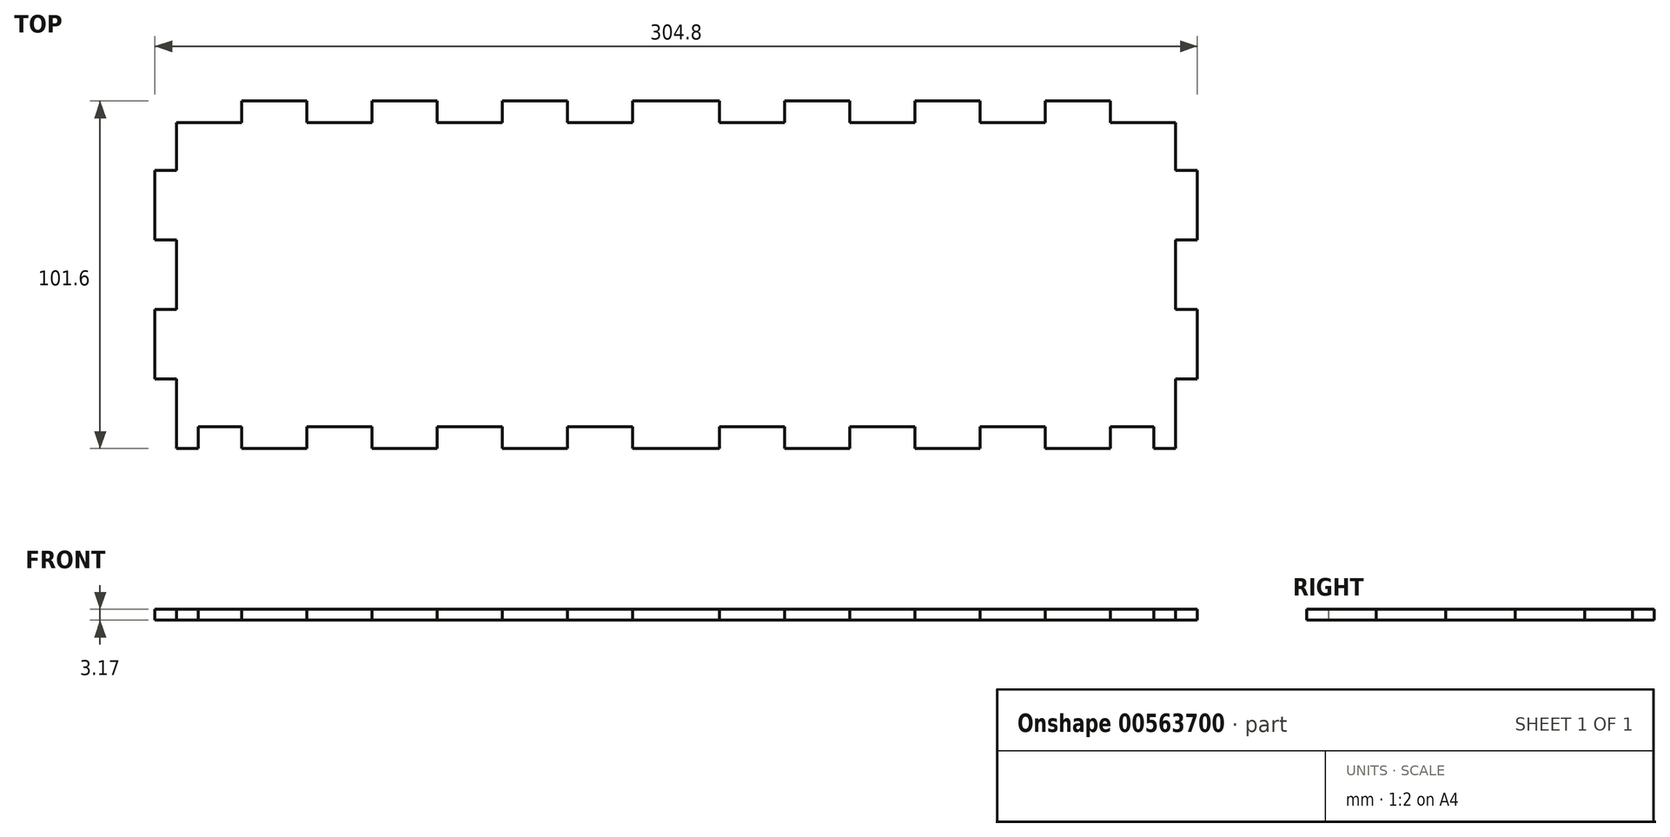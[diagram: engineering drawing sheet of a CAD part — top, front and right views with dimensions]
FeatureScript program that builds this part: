
annotation { "Feature Type Name" : "Feature", "Feature Type Description" : "" }
export const myFeature = defineFeature(function(context is Context, id is Id, definition is map)
    precondition{}
    {
        {
            var Q0;
            Q0=qCreatedBy(makeId("Top.planeOp"),FACE);
            var sketch = newSketch(context, id + "F0", { "sketchPlane" : qUnion([Q0])});
            skLineSegment(sketch, "E0", {"start": v(24.27, -64.8) * mm, "end": v(24.27, -44.49) * mm});
            skLineSegment(sketch, "E1", {"start": v(24.27, -44.49) * mm, "end": v(17.92, -44.49) * mm});
            skLineSegment(sketch, "E2", {"start": v(17.92, -44.49) * mm, "end": v(17.92, -24.17) * mm});
            skLineSegment(sketch, "E3", {"start": v(17.92, -24.17) * mm, "end": v(24.27, -24.17) * mm});
            skLineSegment(sketch, "E4", {"start": v(24.27, -24.17) * mm, "end": v(24.27, -3.85) * mm});
            skLineSegment(sketch, "E5", {"start": v(24.27, -3.85) * mm, "end": v(17.92, -3.85) * mm});
            skLineSegment(sketch, "E6", {"start": v(17.92, -3.85) * mm, "end": v(17.92, 16.47) * mm});
            skLineSegment(sketch, "E7", {"start": v(17.92, 16.47) * mm, "end": v(24.27, 16.47) * mm});
            skLineSegment(sketch, "E8", {"start": v(24.27, 16.47) * mm, "end": v(24.27, 30.44) * mm});
            skLineSegment(sketch, "E9", {"start": v(24.27, 30.44) * mm, "end": v(43.32, 30.44) * mm});
            skLineSegment(sketch, "E10", {"start": v(43.32, 30.44) * mm, "end": v(43.32, 36.8) * mm});
            skLineSegment(sketch, "E11", {"start": v(43.32, 36.8) * mm, "end": v(62.37, 36.8) * mm});
            skLineSegment(sketch, "E12", {"start": v(62.37, 36.8) * mm, "end": v(62.37, 30.44) * mm});
            skLineSegment(sketch, "E13", {"start": v(62.37, 30.44) * mm, "end": v(81.42, 30.44) * mm});
            skLineSegment(sketch, "E14", {"start": v(81.42, 30.44) * mm, "end": v(81.42, 36.8) * mm});
            skLineSegment(sketch, "E15", {"start": v(81.42, 36.8) * mm, "end": v(100.47, 36.8) * mm});
            skLineSegment(sketch, "E16", {"start": v(100.47, 36.8) * mm, "end": v(100.47, 30.44) * mm});
            skLineSegment(sketch, "E17", {"start": v(100.47, 30.44) * mm, "end": v(119.52, 30.44) * mm});
            skLineSegment(sketch, "E18", {"start": v(119.52, 30.44) * mm, "end": v(119.52, 36.8) * mm});
            skLineSegment(sketch, "E19", {"start": v(119.52, 36.8) * mm, "end": v(138.57, 36.8) * mm});
            skLineSegment(sketch, "E20", {"start": v(138.57, 36.8) * mm, "end": v(138.57, 30.44) * mm});
            skLineSegment(sketch, "E21", {"start": v(138.57, 30.44) * mm, "end": v(157.62, 30.44) * mm});
            skLineSegment(sketch, "E22", {"start": v(157.62, 30.44) * mm, "end": v(157.62, 36.8) * mm});
            skLineSegment(sketch, "E23", {"start": v(157.62, 36.8) * mm, "end": v(170.32, 36.8) * mm});
            skLineSegment(sketch, "E24", {"start": v(170.32, 36.8) * mm, "end": v(170.32, -64.8) * mm, "construction": true});
            skLineSegment(sketch, "E25.MirrorCS", {"start": v(240.17, 36.8) * mm, "end": v(240.17, 30.44) * mm});
            skLineSegment(sketch, "E26.MirrorCS", {"start": v(322.72, 16.47) * mm, "end": v(316.37, 16.47) * mm});
            skLineSegment(sketch, "E27.MirrorCS", {"start": v(316.37, -3.85) * mm, "end": v(322.72, -3.85) * mm});
            skLineSegment(sketch, "E28.MirrorCS", {"start": v(221.12, 30.44) * mm, "end": v(221.12, 36.8) * mm});
            skLineSegment(sketch, "E29.MirrorCS", {"start": v(322.72, -24.17) * mm, "end": v(316.37, -24.17) * mm});
            skLineSegment(sketch, "E30.MirrorCS", {"start": v(297.32, 30.44) * mm, "end": v(297.32, 36.8) * mm});
            skLineSegment(sketch, "E31.MirrorCS", {"start": v(202.07, 36.8) * mm, "end": v(202.07, 30.44) * mm});
            skLineSegment(sketch, "E32.MirrorCS", {"start": v(316.37, -44.49) * mm, "end": v(322.72, -44.49) * mm});
            skLineSegment(sketch, "E33.MirrorCS", {"start": v(278.27, 36.8) * mm, "end": v(278.27, 30.44) * mm});
            skLineSegment(sketch, "E34.MirrorCS", {"start": v(183.02, 30.44) * mm, "end": v(183.02, 36.8) * mm});
            skLineSegment(sketch, "E35.MirrorCS", {"start": v(259.22, 30.44) * mm, "end": v(259.22, 36.8) * mm});
            skLineSegment(sketch, "E36.MirrorCS", {"start": v(322.72, -3.85) * mm, "end": v(322.72, 16.47) * mm});
            skLineSegment(sketch, "E37.MirrorCS", {"start": v(316.37, -24.17) * mm, "end": v(316.37, -3.85) * mm});
            skLineSegment(sketch, "E38.MirrorCS", {"start": v(316.37, 16.47) * mm, "end": v(316.37, 30.44) * mm});
            skLineSegment(sketch, "E39.MirrorCS", {"start": v(316.37, 30.44) * mm, "end": v(297.32, 30.44) * mm});
            skLineSegment(sketch, "E40.MirrorCS", {"start": v(322.72, -44.49) * mm, "end": v(322.72, -24.17) * mm});
            skLineSegment(sketch, "E41.MirrorCS", {"start": v(297.32, 36.8) * mm, "end": v(278.27, 36.8) * mm});
            skLineSegment(sketch, "E42.MirrorCS", {"start": v(202.07, 30.44) * mm, "end": v(183.02, 30.44) * mm});
            skLineSegment(sketch, "E43.MirrorCS", {"start": v(259.22, 36.8) * mm, "end": v(240.17, 36.8) * mm});
            skLineSegment(sketch, "E44.MirrorCS", {"start": v(221.12, 36.8) * mm, "end": v(202.07, 36.8) * mm});
            skLineSegment(sketch, "E45.MirrorCS", {"start": v(278.27, 30.44) * mm, "end": v(259.22, 30.44) * mm});
            skLineSegment(sketch, "E46.MirrorCS", {"start": v(316.37, -64.8) * mm, "end": v(316.37, -44.49) * mm});
            skLineSegment(sketch, "E47.MirrorCS", {"start": v(240.17, 30.44) * mm, "end": v(221.12, 30.44) * mm});
            skLineSegment(sketch, "E48.MirrorCS", {"start": v(183.02, 36.8) * mm, "end": v(170.32, 36.8) * mm});
            skLineSegment(sketch, "E49", {"start": v(170.32, -14) * mm, "end": v(26.37, -14) * mm, "construction": true});
            skPoint(sketch, "E49.endSnap0", {"position": v(170.32, -14) * mm});
            skLineSegment(sketch, "E50.MirrorCS", {"start": v(157.62, -64.8) * mm, "end": v(170.32, -64.8) * mm});
            skLineSegment(sketch, "E51.MirrorCS", {"start": v(138.57, -58.46) * mm, "end": v(157.62, -58.46) * mm});
            skLineSegment(sketch, "E52.MirrorCS", {"start": v(119.52, -64.8) * mm, "end": v(138.57, -64.8) * mm});
            skLineSegment(sketch, "E53.MirrorCS", {"start": v(100.47, -58.46) * mm, "end": v(119.52, -58.46) * mm});
            skLineSegment(sketch, "E54.MirrorCS", {"start": v(81.42, -64.8) * mm, "end": v(100.47, -64.8) * mm});
            skLineSegment(sketch, "E55.MirrorCS", {"start": v(157.62, -58.46) * mm, "end": v(157.62, -64.8) * mm});
            skLineSegment(sketch, "E56.MirrorCS", {"start": v(138.57, -64.8) * mm, "end": v(138.57, -58.46) * mm});
            skLineSegment(sketch, "E57.MirrorCS", {"start": v(119.52, -58.46) * mm, "end": v(119.52, -64.8) * mm});
            skLineSegment(sketch, "E58.MirrorCS", {"start": v(100.47, -64.8) * mm, "end": v(100.47, -58.46) * mm});
            skLineSegment(sketch, "E59.MirrorCS", {"start": v(81.42, -58.46) * mm, "end": v(81.42, -64.8) * mm});
            skLineSegment(sketch, "E60.MirrorCS", {"start": v(62.37, -58.46) * mm, "end": v(81.42, -58.46) * mm});
            skLineSegment(sketch, "E61.MirrorCS", {"start": v(62.37, -64.8) * mm, "end": v(62.37, -58.46) * mm});
            skLineSegment(sketch, "E62.MirrorCS", {"start": v(43.32, -64.8) * mm, "end": v(62.37, -64.8) * mm});
            skLineSegment(sketch, "E63.MirrorCS", {"start": v(43.32, -58.46) * mm, "end": v(43.32, -64.8) * mm});
            skLineSegment(sketch, "E64", {"start": v(24.27, -64.8) * mm, "end": v(30.62, -64.8) * mm});
            skLineSegment(sketch, "E65", {"start": v(30.62, -64.8) * mm, "end": v(30.62, -58.46) * mm});
            skLineSegment(sketch, "E66", {"start": v(30.62, -58.46) * mm, "end": v(43.32, -58.46) * mm});
            skLineSegment(sketch, "E67.MirrorCS", {"start": v(316.37, -64.8) * mm, "end": v(310.02, -64.8) * mm});
            skLineSegment(sketch, "E68.MirrorCS", {"start": v(310.02, -64.8) * mm, "end": v(310.02, -58.46) * mm});
            skLineSegment(sketch, "E69.MirrorCS", {"start": v(202.07, -64.8) * mm, "end": v(202.07, -58.46) * mm});
            skLineSegment(sketch, "E70.MirrorCS", {"start": v(183.02, -58.46) * mm, "end": v(183.02, -64.8) * mm});
            skLineSegment(sketch, "E71.MirrorCS", {"start": v(259.22, -58.46) * mm, "end": v(259.22, -64.8) * mm});
            skLineSegment(sketch, "E72.MirrorCS", {"start": v(240.17, -64.8) * mm, "end": v(240.17, -58.46) * mm});
            skLineSegment(sketch, "E73.MirrorCS", {"start": v(278.27, -64.8) * mm, "end": v(278.27, -58.46) * mm});
            skLineSegment(sketch, "E74.MirrorCS", {"start": v(297.32, -58.46) * mm, "end": v(297.32, -64.8) * mm});
            skLineSegment(sketch, "E75.MirrorCS", {"start": v(221.12, -58.46) * mm, "end": v(221.12, -64.8) * mm});
            skLineSegment(sketch, "E76.MirrorCS", {"start": v(278.27, -58.46) * mm, "end": v(259.22, -58.46) * mm});
            skLineSegment(sketch, "E77.MirrorCS", {"start": v(221.12, -64.8) * mm, "end": v(202.07, -64.8) * mm});
            skLineSegment(sketch, "E78.MirrorCS", {"start": v(310.02, -58.46) * mm, "end": v(297.32, -58.46) * mm});
            skLineSegment(sketch, "E79.MirrorCS", {"start": v(297.32, -64.8) * mm, "end": v(278.27, -64.8) * mm});
            skLineSegment(sketch, "E80.MirrorCS", {"start": v(240.17, -58.46) * mm, "end": v(221.12, -58.46) * mm});
            skLineSegment(sketch, "E81.MirrorCS", {"start": v(183.02, -64.8) * mm, "end": v(170.32, -64.8) * mm});
            skLineSegment(sketch, "E82.MirrorCS", {"start": v(202.07, -58.46) * mm, "end": v(183.02, -58.46) * mm});
            skLineSegment(sketch, "E83.MirrorCS", {"start": v(259.22, -64.8) * mm, "end": v(240.17, -64.8) * mm});
            skSolve(sketch);
        }
        {
            var Q0;
            Q0 = qSketchRegion(id + "F0", true);
            extrude(context, id + "F1", {"entities" : qUnion([Q0]), "depth" : 3.17 * mm, "offsetDistance" : 25.4 * mm});
        }
    });
